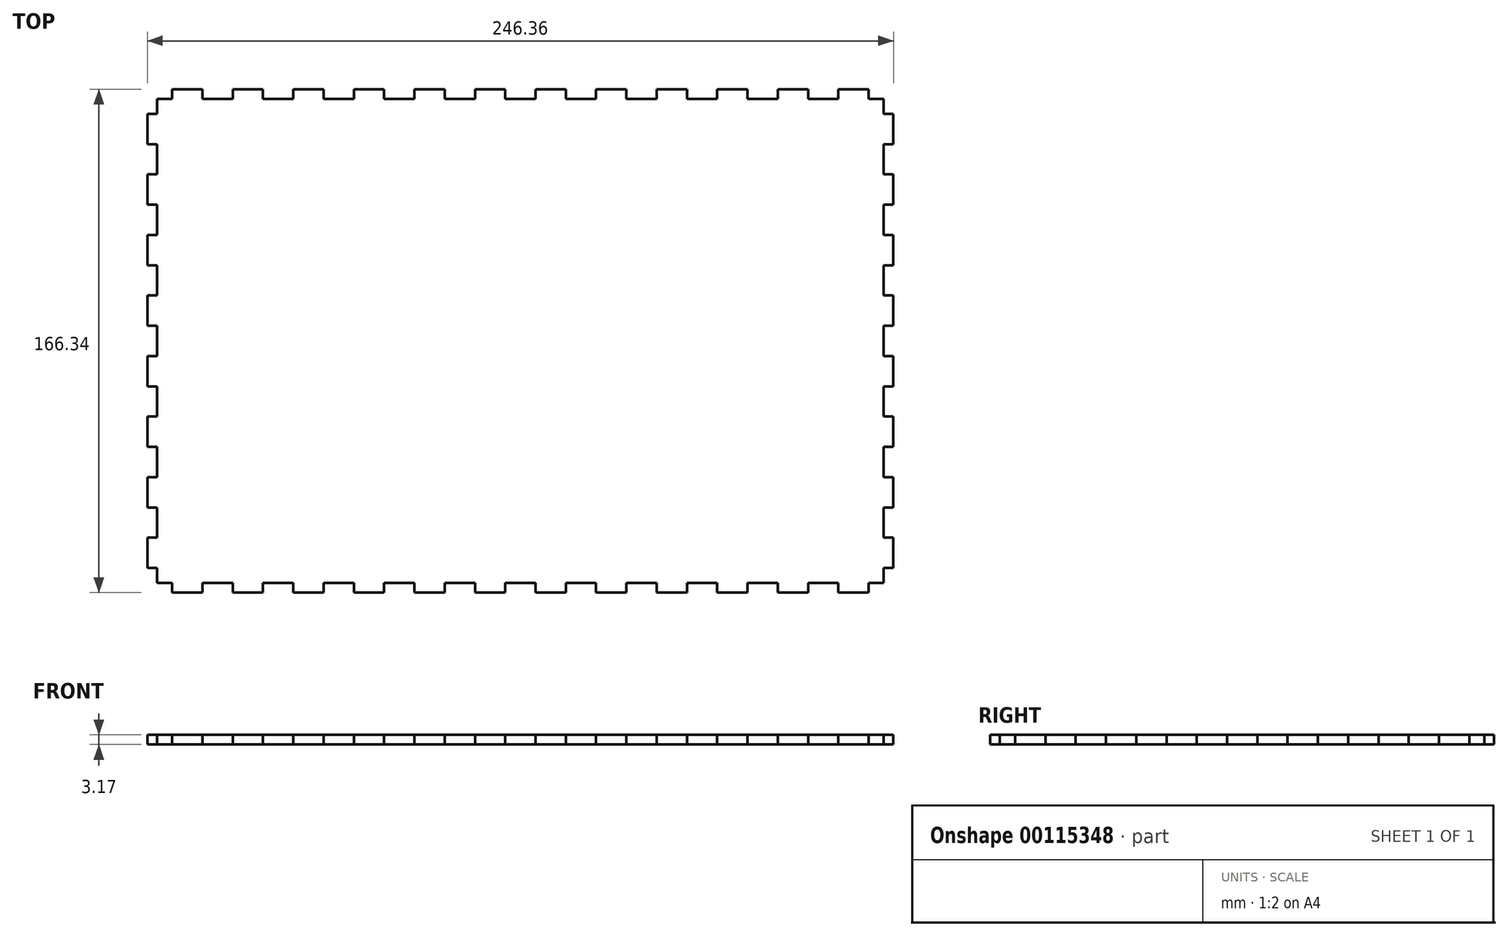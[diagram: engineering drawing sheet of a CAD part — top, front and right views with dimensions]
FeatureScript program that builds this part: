
annotation { "Feature Type Name" : "Feature", "Feature Type Description" : "" }
export const myFeature = defineFeature(function(context is Context, id is Id, definition is map)
    precondition{}
    {
        {
            var Q0;
            Q0=qCreatedBy(makeId("Top.planeOp"),FACE);
            var sketch = newSketch(context, id + "F0", { "sketchPlane" : qUnion([Q0])});
            skLineSegment(sketch, "E0.bottom", {"start": v(0, 0) * mm, "end": v(123.17, 0) * mm, "construction": true});
            skLineSegment(sketch, "E0.top", {"start": v(0, 83.17) * mm, "end": v(123.17, 83.17) * mm, "construction": true});
            skLineSegment(sketch, "E0.left", {"start": v(0, 0) * mm, "end": v(0, 83.17) * mm, "construction": true});
            skLineSegment(sketch, "E0.right", {"start": v(123.17, 0) * mm, "end": v(123.17, 83.17) * mm, "construction": true});
            skLineSegment(sketch, "E1.bottom", {"start": v(0, 0) * mm, "end": v(120, 0) * mm, "construction": true});
            skLineSegment(sketch, "E1.top", {"start": v(0, 80) * mm, "end": v(120, 80) * mm, "construction": true});
            skLineSegment(sketch, "E1.left", {"start": v(0, 0) * mm, "end": v(0, 80) * mm, "construction": true});
            skLineSegment(sketch, "E1.right", {"start": v(120, 0) * mm, "end": v(120, 80) * mm, "construction": true});
            skLineSegment(sketch, "E2", {"start": v(120, 80) * mm, "end": v(115, 80) * mm});
            skLineSegment(sketch, "E3", {"start": v(115, 80) * mm, "end": v(115, 83.17) * mm});
            skLineSegment(sketch, "E4", {"start": v(115, 83.17) * mm, "end": v(105, 83.17) * mm});
            skLineSegment(sketch, "E5", {"start": v(105, 83.17) * mm, "end": v(105, 80) * mm});
            skLineSegment(sketch, "E6", {"start": v(105, 80) * mm, "end": v(95, 80) * mm});
            skLineSegment(sketch, "E7.1.0.0", {"start": v(95, 80) * mm, "end": v(95, 83.17) * mm});
            skLineSegment(sketch, "E7.1.0.1", {"start": v(95, 83.17) * mm, "end": v(85, 83.17) * mm});
            skLineSegment(sketch, "E7.1.0.2", {"start": v(85, 83.17) * mm, "end": v(85, 80) * mm});
            skLineSegment(sketch, "E7.1.0.3", {"start": v(85, 80) * mm, "end": v(75, 80) * mm});
            skLineSegment(sketch, "E7.2.0.0", {"start": v(75, 80) * mm, "end": v(75, 83.17) * mm});
            skLineSegment(sketch, "E7.2.0.1", {"start": v(75, 83.17) * mm, "end": v(65, 83.17) * mm});
            skLineSegment(sketch, "E7.2.0.2", {"start": v(65, 83.17) * mm, "end": v(65, 80) * mm});
            skLineSegment(sketch, "E7.2.0.3", {"start": v(65, 80) * mm, "end": v(55, 80) * mm});
            skLineSegment(sketch, "E7.3.0.0", {"start": v(55, 80) * mm, "end": v(55, 83.17) * mm});
            skLineSegment(sketch, "E7.3.0.1", {"start": v(55, 83.17) * mm, "end": v(45, 83.17) * mm});
            skLineSegment(sketch, "E7.3.0.2", {"start": v(45, 83.17) * mm, "end": v(45, 80) * mm});
            skLineSegment(sketch, "E7.3.0.3", {"start": v(45, 80) * mm, "end": v(35, 80) * mm});
            skLineSegment(sketch, "E7.4.0.0", {"start": v(35, 80) * mm, "end": v(35, 83.17) * mm});
            skLineSegment(sketch, "E7.4.0.1", {"start": v(35, 83.17) * mm, "end": v(25, 83.17) * mm});
            skLineSegment(sketch, "E7.4.0.2", {"start": v(25, 83.17) * mm, "end": v(25, 80) * mm});
            skLineSegment(sketch, "E7.4.0.3", {"start": v(25, 80) * mm, "end": v(15, 80) * mm});
            skLineSegment(sketch, "E7.5.0.0", {"start": v(15, 80) * mm, "end": v(15, 83.17) * mm});
            skLineSegment(sketch, "E7.5.0.1", {"start": v(15, 83.17) * mm, "end": v(5, 83.17) * mm});
            skLineSegment(sketch, "E7.5.0.2", {"start": v(5, 83.17) * mm, "end": v(5, 80) * mm});
            skLineSegment(sketch, "E7.5.0.3", {"start": v(5, 80) * mm, "end": v(0, 80) * mm});
            skLineSegment(sketch, "E8", {"start": v(120, 80) * mm, "end": v(120, 75) * mm});
            skLineSegment(sketch, "E9", {"start": v(120, 75) * mm, "end": v(123.17, 75) * mm});
            skLineSegment(sketch, "E10", {"start": v(123.17, 75) * mm, "end": v(123.17, 65) * mm});
            skLineSegment(sketch, "E11", {"start": v(123.17, 65) * mm, "end": v(120, 65) * mm});
            skLineSegment(sketch, "E12", {"start": v(120, 65) * mm, "end": v(120, 55) * mm});
            skLineSegment(sketch, "E13.0.1.0", {"start": v(120, 55) * mm, "end": v(123.17, 55) * mm});
            skLineSegment(sketch, "E13.0.1.1", {"start": v(123.17, 55) * mm, "end": v(123.17, 45) * mm});
            skLineSegment(sketch, "E13.0.1.2", {"start": v(123.17, 45) * mm, "end": v(120, 45) * mm});
            skLineSegment(sketch, "E13.0.1.3", {"start": v(120, 45) * mm, "end": v(120, 35) * mm});
            skLineSegment(sketch, "E13.0.2.0", {"start": v(120, 35) * mm, "end": v(123.17, 35) * mm});
            skLineSegment(sketch, "E13.0.2.1", {"start": v(123.17, 35) * mm, "end": v(123.17, 25) * mm});
            skLineSegment(sketch, "E13.0.2.2", {"start": v(123.17, 25) * mm, "end": v(120, 25) * mm});
            skLineSegment(sketch, "E13.0.2.3", {"start": v(120, 25) * mm, "end": v(120, 15) * mm});
            skLineSegment(sketch, "E13.0.3.0", {"start": v(120, 15) * mm, "end": v(123.17, 15) * mm});
            skLineSegment(sketch, "E13.0.3.1", {"start": v(123.17, 15) * mm, "end": v(123.17, 5) * mm});
            skLineSegment(sketch, "E13.0.3.2", {"start": v(123.17, 5) * mm, "end": v(120, 5) * mm});
            skLineSegment(sketch, "E13.0.3.3", {"start": v(120, 5) * mm, "end": v(120, 0) * mm});
            skLineSegment(sketch, "E13.direction2", {"start": v(120, 55) * mm, "end": v(120, 35) * mm, "construction": true});
            skLineSegment(sketch, "E14.MirrorCS", {"start": v(-120, 55) * mm, "end": v(-123.17, 55) * mm});
            skLineSegment(sketch, "E15.MirrorCS", {"start": v(-120, 35) * mm, "end": v(-123.17, 35) * mm});
            skLineSegment(sketch, "E16.MirrorCS", {"start": v(-120, 15) * mm, "end": v(-123.17, 15) * mm});
            skLineSegment(sketch, "E17.MirrorCS", {"start": v(-120, 75) * mm, "end": v(-123.17, 75) * mm});
            skLineSegment(sketch, "E18.MirrorCS", {"start": v(-120, 80) * mm, "end": v(-120, 75) * mm});
            skLineSegment(sketch, "E19.MirrorCS", {"start": v(-65, 83.17) * mm, "end": v(-65, 80) * mm});
            skLineSegment(sketch, "E20.MirrorCS", {"start": v(-95, 80) * mm, "end": v(-95, 83.17) * mm});
            skLineSegment(sketch, "E21.MirrorCS", {"start": v(-85, 83.17) * mm, "end": v(-85, 80) * mm});
            skLineSegment(sketch, "E22.MirrorCS", {"start": v(-55, 80) * mm, "end": v(-55, 83.17) * mm});
            skLineSegment(sketch, "E23.MirrorCS", {"start": v(-123.17, 45) * mm, "end": v(-120, 45) * mm});
            skLineSegment(sketch, "E24.MirrorCS", {"start": v(-123.17, 25) * mm, "end": v(-120, 25) * mm});
            skLineSegment(sketch, "E25.MirrorCS", {"start": v(-105, 83.17) * mm, "end": v(-105, 80) * mm});
            skLineSegment(sketch, "E26.MirrorCS", {"start": v(-123.17, 65) * mm, "end": v(-120, 65) * mm});
            skLineSegment(sketch, "E27.MirrorCS", {"start": v(-115, 80) * mm, "end": v(-115, 83.17) * mm});
            skLineSegment(sketch, "E28.MirrorCS", {"start": v(-120, 80) * mm, "end": v(-115, 80) * mm});
            skLineSegment(sketch, "E29.MirrorCS", {"start": v(-5, 83.17) * mm, "end": v(-5, 80) * mm});
            skLineSegment(sketch, "E30.MirrorCS", {"start": v(-123.17, 5) * mm, "end": v(-120, 5) * mm});
            skLineSegment(sketch, "E31.MirrorCS", {"start": v(-120, 5) * mm, "end": v(-120, 0) * mm});
            skLineSegment(sketch, "E32.MirrorCS", {"start": v(-75, 80) * mm, "end": v(-75, 83.17) * mm});
            skLineSegment(sketch, "E33.MirrorCS", {"start": v(-25, 83.17) * mm, "end": v(-25, 80) * mm});
            skLineSegment(sketch, "E34.MirrorCS", {"start": v(-45, 83.17) * mm, "end": v(-45, 80) * mm});
            skLineSegment(sketch, "E35.MirrorCS", {"start": v(-35, 80) * mm, "end": v(-35, 83.17) * mm});
            skLineSegment(sketch, "E36.MirrorCS", {"start": v(-5, 80) * mm, "end": v(0, 80) * mm});
            skLineSegment(sketch, "E37.MirrorCS", {"start": v(-15, 80) * mm, "end": v(-15, 83.17) * mm});
            skLineSegment(sketch, "E38.MirrorCS", {"start": v(-120, 55) * mm, "end": v(-120, 35) * mm, "construction": true});
            skLineSegment(sketch, "E39.MirrorCS", {"start": v(0, 0) * mm, "end": v(-123.17, 0) * mm, "construction": true});
            skLineSegment(sketch, "E40.MirrorCS", {"start": v(-105, 80) * mm, "end": v(-95, 80) * mm});
            skLineSegment(sketch, "E41.MirrorCS", {"start": v(-35, 83.17) * mm, "end": v(-25, 83.17) * mm});
            skLineSegment(sketch, "E42.MirrorCS", {"start": v(-123.17, 75) * mm, "end": v(-123.17, 65) * mm});
            skLineSegment(sketch, "E43.MirrorCS", {"start": v(-95, 83.17) * mm, "end": v(-85, 83.17) * mm});
            skLineSegment(sketch, "E44.MirrorCS", {"start": v(0, 83.17) * mm, "end": v(-123.17, 83.17) * mm, "construction": true});
            skLineSegment(sketch, "E45.MirrorCS", {"start": v(-123.17, 0) * mm, "end": v(-123.17, 83.17) * mm, "construction": true});
            skLineSegment(sketch, "E46.MirrorCS", {"start": v(0, 0) * mm, "end": v(-120, 0) * mm, "construction": true});
            skLineSegment(sketch, "E47.MirrorCS", {"start": v(-45, 80) * mm, "end": v(-35, 80) * mm});
            skLineSegment(sketch, "E48.MirrorCS", {"start": v(-25, 80) * mm, "end": v(-15, 80) * mm});
            skLineSegment(sketch, "E49.MirrorCS", {"start": v(-120, 65) * mm, "end": v(-120, 55) * mm});
            skLineSegment(sketch, "E50.MirrorCS", {"start": v(-15, 83.17) * mm, "end": v(-5, 83.17) * mm});
            skLineSegment(sketch, "E51.MirrorCS", {"start": v(-75, 83.17) * mm, "end": v(-65, 83.17) * mm});
            skLineSegment(sketch, "E52.MirrorCS", {"start": v(-85, 80) * mm, "end": v(-75, 80) * mm});
            skLineSegment(sketch, "E53.MirrorCS", {"start": v(-123.17, 15) * mm, "end": v(-123.17, 5) * mm});
            skLineSegment(sketch, "E54.MirrorCS", {"start": v(-115, 83.17) * mm, "end": v(-105, 83.17) * mm});
            skLineSegment(sketch, "E55.MirrorCS", {"start": v(-120, 0) * mm, "end": v(-120, 80) * mm, "construction": true});
            skLineSegment(sketch, "E56.MirrorCS", {"start": v(0, 80) * mm, "end": v(-120, 80) * mm, "construction": true});
            skLineSegment(sketch, "E57.MirrorCS", {"start": v(-123.17, 35) * mm, "end": v(-123.17, 25) * mm});
            skLineSegment(sketch, "E58.MirrorCS", {"start": v(-123.17, 55) * mm, "end": v(-123.17, 45) * mm});
            skLineSegment(sketch, "E59.MirrorCS", {"start": v(-120, 45) * mm, "end": v(-120, 35) * mm});
            skLineSegment(sketch, "E60.MirrorCS", {"start": v(-55, 83.17) * mm, "end": v(-45, 83.17) * mm});
            skLineSegment(sketch, "E61.MirrorCS", {"start": v(-120, 25) * mm, "end": v(-120, 15) * mm});
            skLineSegment(sketch, "E62.MirrorCS", {"start": v(-65, 80) * mm, "end": v(-55, 80) * mm});
            skLineSegment(sketch, "E63.MirrorCS", {"start": v(-5, -80) * mm, "end": v(0, -80) * mm});
            skLineSegment(sketch, "E64.MirrorCS", {"start": v(-5, -83.17) * mm, "end": v(-5, -80) * mm});
            skLineSegment(sketch, "E65.MirrorCS", {"start": v(120, -80) * mm, "end": v(120, -75) * mm});
            skLineSegment(sketch, "E66.MirrorCS", {"start": v(115, -80) * mm, "end": v(115, -83.17) * mm});
            skLineSegment(sketch, "E67.MirrorCS", {"start": v(120, -80) * mm, "end": v(115, -80) * mm});
            skLineSegment(sketch, "E68.MirrorCS", {"start": v(120, -55) * mm, "end": v(123.17, -55) * mm});
            skLineSegment(sketch, "E69.MirrorCS", {"start": v(-120, -35) * mm, "end": v(-123.17, -35) * mm});
            skLineSegment(sketch, "E70.MirrorCS", {"start": v(-120, -55) * mm, "end": v(-123.17, -55) * mm});
            skLineSegment(sketch, "E71.MirrorCS", {"start": v(120, -35) * mm, "end": v(123.17, -35) * mm});
            skLineSegment(sketch, "E72.MirrorCS", {"start": v(120, -15) * mm, "end": v(123.17, -15) * mm});
            skLineSegment(sketch, "E73.MirrorCS", {"start": v(120, -75) * mm, "end": v(123.17, -75) * mm});
            skLineSegment(sketch, "E74.MirrorCS", {"start": v(35, -80) * mm, "end": v(35, -83.17) * mm});
            skLineSegment(sketch, "E75.MirrorCS", {"start": v(-95, -80) * mm, "end": v(-95, -83.17) * mm});
            skLineSegment(sketch, "E76.MirrorCS", {"start": v(120, -5) * mm, "end": v(120, 0) * mm});
            skLineSegment(sketch, "E77.MirrorCS", {"start": v(-120, -80) * mm, "end": v(-115, -80) * mm});
            skLineSegment(sketch, "E78.MirrorCS", {"start": v(75, -80) * mm, "end": v(75, -83.17) * mm});
            skLineSegment(sketch, "E79.MirrorCS", {"start": v(-35, -80) * mm, "end": v(-35, -83.17) * mm});
            skLineSegment(sketch, "E80.MirrorCS", {"start": v(123.17, -45) * mm, "end": v(120, -45) * mm});
            skLineSegment(sketch, "E81.MirrorCS", {"start": v(-65, -83.17) * mm, "end": v(-65, -80) * mm});
            skLineSegment(sketch, "E82.MirrorCS", {"start": v(5, -80) * mm, "end": v(0, -80) * mm});
            skLineSegment(sketch, "E83.MirrorCS", {"start": v(123.17, -5) * mm, "end": v(120, -5) * mm});
            skLineSegment(sketch, "E84.MirrorCS", {"start": v(-115, -80) * mm, "end": v(-115, -83.17) * mm});
            skLineSegment(sketch, "E85.MirrorCS", {"start": v(-45, -83.17) * mm, "end": v(-45, -80) * mm});
            skLineSegment(sketch, "E86.MirrorCS", {"start": v(45, -83.17) * mm, "end": v(45, -80) * mm});
            skLineSegment(sketch, "E87.MirrorCS", {"start": v(-120, -80) * mm, "end": v(-120, -75) * mm});
            skLineSegment(sketch, "E88.MirrorCS", {"start": v(105, -83.17) * mm, "end": v(105, -80) * mm});
            skLineSegment(sketch, "E89.MirrorCS", {"start": v(85, -83.17) * mm, "end": v(85, -80) * mm});
            skLineSegment(sketch, "E90.MirrorCS", {"start": v(5, -83.17) * mm, "end": v(5, -80) * mm});
            skLineSegment(sketch, "E91.MirrorCS", {"start": v(95, -80) * mm, "end": v(95, -83.17) * mm});
            skLineSegment(sketch, "E92.MirrorCS", {"start": v(-123.17, -65) * mm, "end": v(-120, -65) * mm});
            skLineSegment(sketch, "E93.MirrorCS", {"start": v(-120, -75) * mm, "end": v(-123.17, -75) * mm});
            skLineSegment(sketch, "E94.MirrorCS", {"start": v(-25, -83.17) * mm, "end": v(-25, -80) * mm});
            skLineSegment(sketch, "E95.MirrorCS", {"start": v(123.17, -65) * mm, "end": v(120, -65) * mm});
            skLineSegment(sketch, "E96.MirrorCS", {"start": v(15, -80) * mm, "end": v(15, -83.17) * mm});
            skLineSegment(sketch, "E97.MirrorCS", {"start": v(-120, -5) * mm, "end": v(-120, 0) * mm});
            skLineSegment(sketch, "E98.MirrorCS", {"start": v(-123.17, -25) * mm, "end": v(-120, -25) * mm});
            skLineSegment(sketch, "E99.MirrorCS", {"start": v(0, 0) * mm, "end": v(0, -83.17) * mm, "construction": true});
            skLineSegment(sketch, "E100.MirrorCS", {"start": v(-105, -83.17) * mm, "end": v(-105, -80) * mm});
            skLineSegment(sketch, "E101.MirrorCS", {"start": v(-123.17, -45) * mm, "end": v(-120, -45) * mm});
            skLineSegment(sketch, "E102.MirrorCS", {"start": v(123.17, -25) * mm, "end": v(120, -25) * mm});
            skLineSegment(sketch, "E103.MirrorCS", {"start": v(-55, -80) * mm, "end": v(-55, -83.17) * mm});
            skLineSegment(sketch, "E104.MirrorCS", {"start": v(-15, -80) * mm, "end": v(-15, -83.17) * mm});
            skLineSegment(sketch, "E105.MirrorCS", {"start": v(55, -80) * mm, "end": v(55, -83.17) * mm});
            skLineSegment(sketch, "E106.MirrorCS", {"start": v(65, -83.17) * mm, "end": v(65, -80) * mm});
            skLineSegment(sketch, "E107.MirrorCS", {"start": v(-123.17, -5) * mm, "end": v(-120, -5) * mm});
            skLineSegment(sketch, "E108.MirrorCS", {"start": v(25, -83.17) * mm, "end": v(25, -80) * mm});
            skLineSegment(sketch, "E109.MirrorCS", {"start": v(-85, -83.17) * mm, "end": v(-85, -80) * mm});
            skLineSegment(sketch, "E110.MirrorCS", {"start": v(-75, -80) * mm, "end": v(-75, -83.17) * mm});
            skLineSegment(sketch, "E111.MirrorCS", {"start": v(-120, -15) * mm, "end": v(-123.17, -15) * mm});
            skLineSegment(sketch, "E112.MirrorCS", {"start": v(-15, -83.17) * mm, "end": v(-5, -83.17) * mm});
            skLineSegment(sketch, "E113.MirrorCS", {"start": v(105, -80) * mm, "end": v(95, -80) * mm});
            skLineSegment(sketch, "E114.MirrorCS", {"start": v(115, -83.17) * mm, "end": v(105, -83.17) * mm});
            skLineSegment(sketch, "E115.MirrorCS", {"start": v(120, -25) * mm, "end": v(120, -15) * mm});
            skLineSegment(sketch, "E116.MirrorCS", {"start": v(-120, -55) * mm, "end": v(-120, -35) * mm, "construction": true});
            skLineSegment(sketch, "E117.MirrorCS", {"start": v(-55, -83.17) * mm, "end": v(-45, -83.17) * mm});
            skLineSegment(sketch, "E118.MirrorCS", {"start": v(120, -55) * mm, "end": v(120, -35) * mm, "construction": true});
            skLineSegment(sketch, "E119.MirrorCS", {"start": v(0, -83.17) * mm, "end": v(-123.17, -83.17) * mm, "construction": true});
            skLineSegment(sketch, "E120.MirrorCS", {"start": v(75, -83.17) * mm, "end": v(65, -83.17) * mm});
            skLineSegment(sketch, "E121.MirrorCS", {"start": v(-75, -83.17) * mm, "end": v(-65, -83.17) * mm});
            skLineSegment(sketch, "E122.MirrorCS", {"start": v(120, -45) * mm, "end": v(120, -35) * mm});
            skLineSegment(sketch, "E123.MirrorCS", {"start": v(-120, -45) * mm, "end": v(-120, -35) * mm});
            skLineSegment(sketch, "E124.MirrorCS", {"start": v(-95, -83.17) * mm, "end": v(-85, -83.17) * mm});
            skLineSegment(sketch, "E125.MirrorCS", {"start": v(45, -80) * mm, "end": v(35, -80) * mm});
            skLineSegment(sketch, "E126.MirrorCS", {"start": v(-123.17, -75) * mm, "end": v(-123.17, -65) * mm});
            skLineSegment(sketch, "E127.MirrorCS", {"start": v(85, -80) * mm, "end": v(75, -80) * mm});
            skLineSegment(sketch, "E128.MirrorCS", {"start": v(-120, -65) * mm, "end": v(-120, -55) * mm});
            skLineSegment(sketch, "E129.MirrorCS", {"start": v(123.17, -55) * mm, "end": v(123.17, -45) * mm});
            skLineSegment(sketch, "E130.MirrorCS", {"start": v(-123.17, -55) * mm, "end": v(-123.17, -45) * mm});
            skLineSegment(sketch, "E131.MirrorCS", {"start": v(120, 0) * mm, "end": v(120, -80) * mm, "construction": true});
            skLineSegment(sketch, "E132.MirrorCS", {"start": v(0, 0) * mm, "end": v(0, -80) * mm, "construction": true});
            skLineSegment(sketch, "E133.MirrorCS", {"start": v(0, -80) * mm, "end": v(120, -80) * mm, "construction": true});
            skLineSegment(sketch, "E134.MirrorCS", {"start": v(123.17, 0) * mm, "end": v(123.17, -83.17) * mm, "construction": true});
            skLineSegment(sketch, "E135.MirrorCS", {"start": v(0, -83.17) * mm, "end": v(123.17, -83.17) * mm, "construction": true});
            skLineSegment(sketch, "E136.MirrorCS", {"start": v(95, -83.17) * mm, "end": v(85, -83.17) * mm});
            skLineSegment(sketch, "E137.MirrorCS", {"start": v(-123.17, -35) * mm, "end": v(-123.17, -25) * mm});
            skLineSegment(sketch, "E138.MirrorCS", {"start": v(123.17, -15) * mm, "end": v(123.17, -5) * mm});
            skLineSegment(sketch, "E139.MirrorCS", {"start": v(-35, -83.17) * mm, "end": v(-25, -83.17) * mm});
            skLineSegment(sketch, "E140.MirrorCS", {"start": v(55, -83.17) * mm, "end": v(45, -83.17) * mm});
            skLineSegment(sketch, "E141.MirrorCS", {"start": v(0, -80) * mm, "end": v(-120, -80) * mm, "construction": true});
            skLineSegment(sketch, "E142.MirrorCS", {"start": v(65, -80) * mm, "end": v(55, -80) * mm});
            skLineSegment(sketch, "E143.MirrorCS", {"start": v(-85, -80) * mm, "end": v(-75, -80) * mm});
            skLineSegment(sketch, "E144.MirrorCS", {"start": v(25, -80) * mm, "end": v(15, -80) * mm});
            skLineSegment(sketch, "E145.MirrorCS", {"start": v(-45, -80) * mm, "end": v(-35, -80) * mm});
            skLineSegment(sketch, "E146.MirrorCS", {"start": v(-25, -80) * mm, "end": v(-15, -80) * mm});
            skLineSegment(sketch, "E147.MirrorCS", {"start": v(123.17, -75) * mm, "end": v(123.17, -65) * mm});
            skLineSegment(sketch, "E148.MirrorCS", {"start": v(35, -83.17) * mm, "end": v(25, -83.17) * mm});
            skLineSegment(sketch, "E149.MirrorCS", {"start": v(-65, -80) * mm, "end": v(-55, -80) * mm});
            skLineSegment(sketch, "E150.MirrorCS", {"start": v(-120, -25) * mm, "end": v(-120, -15) * mm});
            skLineSegment(sketch, "E151.MirrorCS", {"start": v(-115, -83.17) * mm, "end": v(-105, -83.17) * mm});
            skLineSegment(sketch, "E152.MirrorCS", {"start": v(123.17, -35) * mm, "end": v(123.17, -25) * mm});
            skLineSegment(sketch, "E153.MirrorCS", {"start": v(-120, 0) * mm, "end": v(-120, -80) * mm, "construction": true});
            skLineSegment(sketch, "E154.MirrorCS", {"start": v(-123.17, 0) * mm, "end": v(-123.17, -83.17) * mm, "construction": true});
            skLineSegment(sketch, "E155.MirrorCS", {"start": v(120, -65) * mm, "end": v(120, -55) * mm});
            skLineSegment(sketch, "E156.MirrorCS", {"start": v(15, -83.17) * mm, "end": v(5, -83.17) * mm});
            skLineSegment(sketch, "E157.MirrorCS", {"start": v(-123.17, -15) * mm, "end": v(-123.17, -5) * mm});
            skLineSegment(sketch, "E158.MirrorCS", {"start": v(-105, -80) * mm, "end": v(-95, -80) * mm});
            skSolve(sketch);
        }
        {
            var Q0;
            Q0=makeQuery(id+"F0.imprint","IMPRINT",FACE,{"disambiguationData":[TD([[makeQuery(id+"F0.imprint","IMPRINT",EDGE,{"derivedFrom":sQuery(id+"F0.wireOp",EDGE,"E2")}),1.0]])]});
            extrude(context, id + "F1", {"entities" : qUnion([Q0]), "depth" : 3.17 * mm});
        }
    });
